# Revit family: CADS_AIRFLOWdev_Airvalve_FireProtection125mm_Extract
name_source: partatom
category: Air Terminals
revit_build: Autodesk Revit 2015 (Build: 20160512_1515(x64)
units: mm (PartAtom-declared; Revit-internal decimal feet)

## types (1)
- CADS_AIRFLOWdev_Airvalve_FireProtection125mm_Extract
    6MonthlyMaintenance = Visually inspect system, clean the fan and ducting if necessary
    A = 175 mm  [stored 0.574147 ft]
    A1 = 100 mm  [stored 0.328084 ft]
    AssemblyPlace = UNKNOWN
    AssetType = FIXED
    B = 75 mm
    B1 = 20 mm  [stored 0.0656168 ft]
    CADS_Index = 0
    CEApproval = Yes
    Color = White
    Constituents = Fire Protection Extract Valve
    Default Elevation = 1219 mm
    DuctDiameter = 125 mm  [stored 0.410105 ft]
    DurationUnit = Year
    ExpectedServiceLife = 10
    Features = Fire Protection Extract Valve
    Finish = Zinc powder coated
    FireControlPanelLinks = No
    Fitting Type = Ignore
    Grade = Virgin
    GrossWeight = 0.20 kg
    ISO140001 = Yes
    ISO90001 = Yes
    IsExtendedWarranty = No
    Manufacturer = Airflow Developments Ltd
    ManufacturerAddress = Aidelle House
Lancaster Road
Cressex Business Park
High Wycombe
Bucks
HP123QP
    ManufacturerTelephone = 01494 525252
    ManufacturerWebsite = www.airflow.com
    Material = Steel
    NBSCode = 90-75-50/370 Air terminals;
    NominalHeight = 75 mm
    NominalLength = 175 mm  [stored 0.574147 ft]
    NominalWidth = 175 mm  [stored 0.574147 ft]
    PassiveHouseApproval = No
    PointOfContact = Airflow Developments Ltd
    ProductLiterature = https://www.airflow.com
    ProductionYear = 2017
    Quantity = 1
    RedDotDesignAward = No
    ReplacementCost = 145.932
    RunID = 0
    SAPApproval = Yes
    ServiceLifeDuration = 10
    ServiceLifeType = EXPECTEDSERVICELIFE
    Shape = Round
    ShippingWeight = 0.24 kg
    Size = 75 x 175 x 175
    Status = New
    TemperatureRange = up to 72°C
    Uniclass2015 = Pr_65_70_46_07
    WarrantyGuarantor = Airflow Developments Ltd
    WarrantyPeriod = 0

note: [stored X ft] marks values corroborated as IEEE doubles in the binary element streams (Revit-internal decimal feet)

## geometry (parser evidence)
native form markers: Blend x2, Sweep x3
no freeform markers — native parametric forms only
